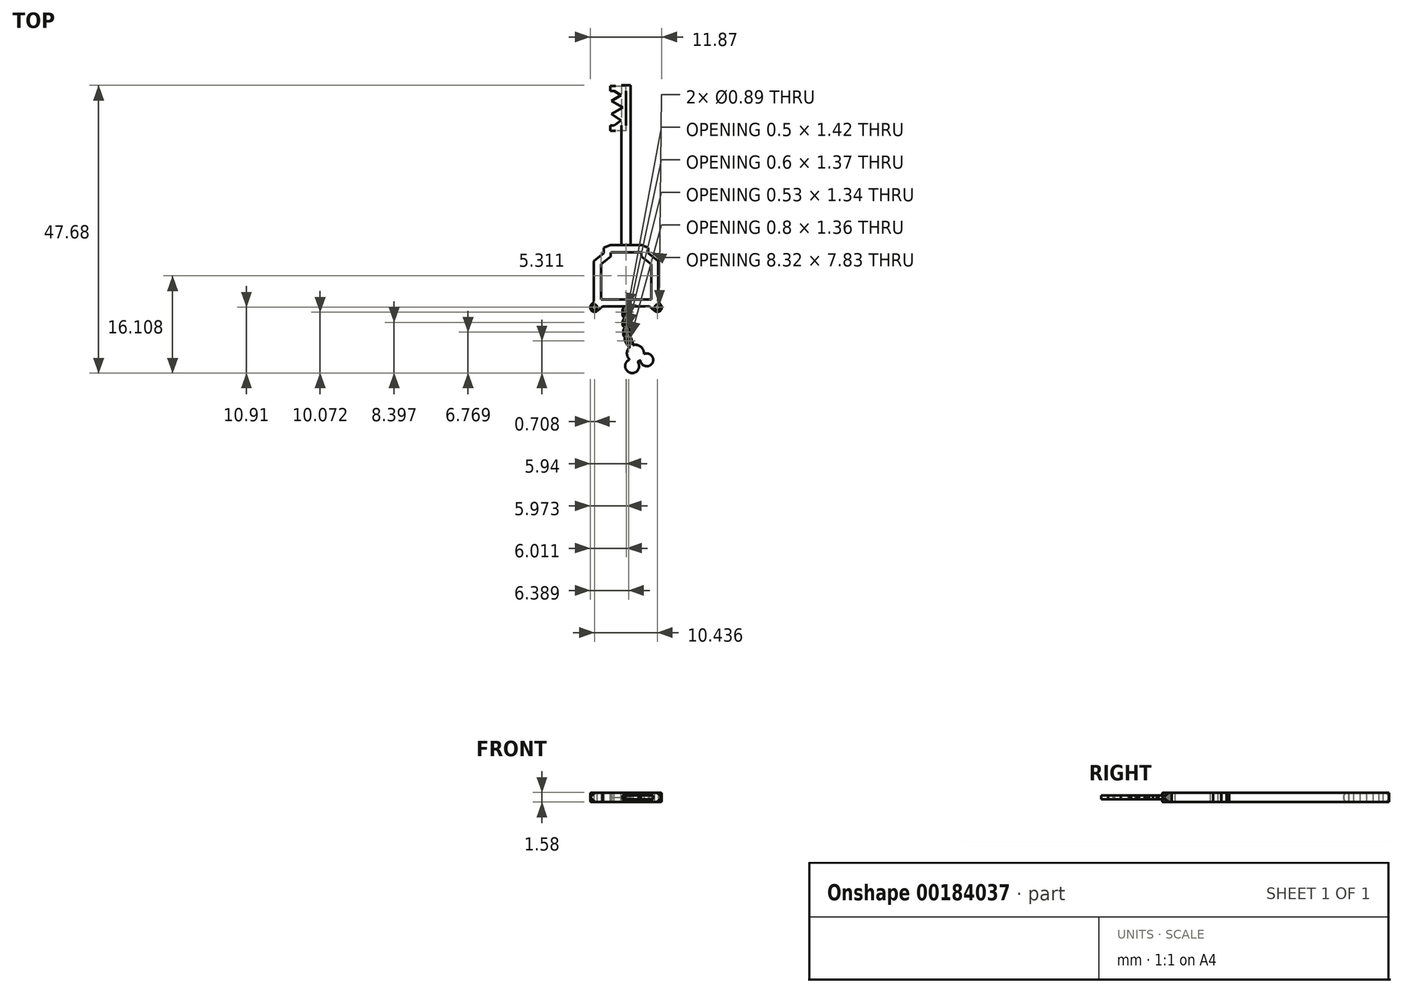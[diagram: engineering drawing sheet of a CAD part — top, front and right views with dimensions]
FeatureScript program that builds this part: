
annotation { "Feature Type Name" : "Feature", "Feature Type Description" : "" }
export const myFeature = defineFeature(function(context is Context, id is Id, definition is map)
    precondition{}
    {
        {
            var Q0;
            Q0=qCreatedBy(makeId("Top.planeOp"),FACE);
            var sketch = newSketch(context, id + "F0", { "sketchPlane" : qUnion([Q0])});
            skLineSegment(sketch, "E0.bottom", {"start": v(0, 26.39) * mm, "end": v(-3.39, 26.39) * mm});
            skLineSegment(sketch, "E0.top", {"start": v(0, 18.97) * mm, "end": v(-3.39, 18.97) * mm});
            skLineSegment(sketch, "E0.left", {"start": v(0, 26.39) * mm, "end": v(0, 18.97) * mm});
            skLineSegment(sketch, "E0.right", {"start": v(-3.39, 26.39) * mm, "end": v(-3.39, 18.97) * mm});
            skSolve(sketch);
        }
        {
            var Q0;
            Q0=makeQuery(id+"F0.imprint","IMPRINT",FACE,{"disambiguationData":[TD([[makeQuery(id+"F0.imprint","IMPRINT",EDGE,{"derivedFrom":sQuery(id+"F0.wireOp",EDGE,"E0.bottom")}),1.0]])]});
            extrude(context, id + "F1", {"entities" : qUnion([Q0]), "endBound" : BoundingType.SYMMETRIC, "depth" : 1.57 * mm});
        }
        {
            var Q0;
            Q0=makeQuery(id+"F1.opExtrude","CAP_EDGE",EDGE,{"disambiguationData":[OSD([sQuery(id+"F0.wireOp",EDGE,"E0.top")])],"isStart":false});
            var Q1;
            Q1=makeQuery(id+"F1.opExtrude","CAP_EDGE",EDGE,{"disambiguationData":[OSD([sQuery(id+"F0.wireOp",EDGE,"E0.top")])],"isStart":true});
            var Q2;
            Q2=makeQuery(id+"F1.opExtrude","CAP_EDGE",EDGE,{"disambiguationData":[OSD([sQuery(id+"F0.wireOp",EDGE,"E0.bottom")])],"isStart":false});
            var Q3;
            Q3=makeQuery(id+"F1.opExtrude","CAP_EDGE",EDGE,{"disambiguationData":[OSD([sQuery(id+"F0.wireOp",EDGE,"E0.bottom")])],"isStart":true});
            fillet(context, id + "F2", {"entities" : qUnion([Q0, Q1, Q2, Q3]), "radius" : 0.86 * mm, "tangentPropagation" : true, "rho" : 0.5, "crossSection" : FilletCrossSection.CONIC, "allowEdgeOverflow" : false});
        }
        {
            var Q0;
            Q0=makeQuery(id+"F1.opExtrude","CAP_FACE",FACE,{"disambiguationData":[OSD([sQuery(id+"F0.wireOp",EDGE,"E0.bottom"),sQuery(id+"F0.wireOp",EDGE,"E0.top"),sQuery(id+"F0.wireOp",EDGE,"E0.left"),sQuery(id+"F0.wireOp",EDGE,"E0.right")])],"isStart":false});
            var sketch = newSketch(context, id + "F3", { "sketchPlane" : qUnion([Q0])});
            skLineSegment(sketch, "E1", {"start": v(-3.39, 25.53) * mm, "end": v(-1.97, 25.53) * mm});
            skLineSegment(sketch, "E2", {"start": v(-1.97, 25.53) * mm, "end": v(-0.83, 24.86) * mm});
            skLineSegment(sketch, "E3", {"start": v(-0.83, 24.86) * mm, "end": v(-2.39, 23.92) * mm});
            skLineSegment(sketch, "E4", {"start": v(-2.39, 23.92) * mm, "end": v(-0.52, 22.82) * mm});
            skLineSegment(sketch, "E5", {"start": v(-0.52, 22.82) * mm, "end": v(-2.39, 21.74) * mm});
            skLineSegment(sketch, "E6", {"start": v(-2.39, 21.74) * mm, "end": v(-0.83, 20.67) * mm});
            skLineSegment(sketch, "E7", {"start": v(-0.83, 20.67) * mm, "end": v(-2, 19.83) * mm});
            skLineSegment(sketch, "E8", {"start": v(-2, 19.83) * mm, "end": v(-3.39, 19.83) * mm});
            skLineSegment(sketch, "E9", {"start": v(-3.39, 19.83) * mm, "end": v(-3.39, 25.53) * mm});
            skSolve(sketch);
        }
        {
            var Q0;
            Q0=makeQuery(id+"F3.imprint","IMPRINT",FACE,{"disambiguationData":[TD([[makeQuery(id+"F3.imprint","IMPRINT",EDGE,{"derivedFrom":sQuery(id+"F3.wireOp",EDGE,"E1")}),1.0]])]});
            extrude(context, id + "F4", {"entities" : qUnion([Q0]), "operationType" : NewBodyOperationType.REMOVE, "oppositeDirection" : true, "depth" : 2.54 * mm});
        }
        {
            var Q0;
            Q0=qCreatedBy(makeId("Top.planeOp"),FACE);
            var sketch = newSketch(context, id + "F5", { "sketchPlane" : qUnion([Q0])});
            skLineSegment(sketch, "E10", {"start": v(0, 0) * mm, "end": v(-2.6, 0) * mm});
            skLineSegment(sketch, "E11", {"start": v(-2.6, 0) * mm, "end": v(-3.7, -0.44) * mm});
            skLineSegment(sketch, "E12", {"start": v(-3.7, -0.44) * mm, "end": v(-3.7, -1.33) * mm});
            skLineSegment(sketch, "E13", {"start": v(-3.7, -1.33) * mm, "end": v(-5.33, -2.62) * mm});
            skLineSegment(sketch, "E14", {"start": v(-5.33, -2.62) * mm, "end": v(-5.33, -9.54) * mm});
            skLineSegment(sketch, "E15", {"start": v(-5.33, -9.54) * mm, "end": v(-6.2, -10.17) * mm});
            skLineSegment(sketch, "E16", {"start": v(-6.2, -10.17) * mm, "end": v(-5.33, -11.38) * mm});
            skLineSegment(sketch, "E17", {"start": v(-5.33, -11.38) * mm, "end": v(-3.9, -10.17) * mm});
            skLineSegment(sketch, "E18", {"start": v(-3.9, -10.17) * mm, "end": v(0, -10.17) * mm});
            skLineSegment(sketch, "E19.MirrorCS", {"start": v(2.6, 0) * mm, "end": v(3.7, -0.44) * mm});
            skLineSegment(sketch, "E20.MirrorCS", {"start": v(3.7, -0.44) * mm, "end": v(3.7, -1.33) * mm});
            skLineSegment(sketch, "E21.MirrorCS", {"start": v(3.7, -1.33) * mm, "end": v(5.33, -2.62) * mm});
            skLineSegment(sketch, "E22.MirrorCS", {"start": v(5.33, -2.62) * mm, "end": v(5.33, -9.54) * mm});
            skLineSegment(sketch, "E23.MirrorCS", {"start": v(5.33, -9.54) * mm, "end": v(6.2, -10.17) * mm});
            skLineSegment(sketch, "E24.MirrorCS", {"start": v(6.2, -10.17) * mm, "end": v(5.33, -11.38) * mm});
            skLineSegment(sketch, "E25.MirrorCS", {"start": v(5.33, -11.38) * mm, "end": v(3.9, -10.17) * mm});
            skLineSegment(sketch, "E26.MirrorCS", {"start": v(3.9, -10.17) * mm, "end": v(0, -10.17) * mm});
            skLineSegment(sketch, "E27.MirrorCS", {"start": v(0, 0) * mm, "end": v(2.6, 0) * mm});
            skLineSegment(sketch, "E28.0", {"start": v(2.52, -1.17) * mm, "end": v(2.52, -1.9) * mm});
            skLineSegment(sketch, "E28.1", {"start": v(-2.52, -1.23) * mm, "end": v(-2.52, -1.9) * mm});
            skLineSegment(sketch, "E28.2", {"start": v(-2.37, -1.17) * mm, "end": v(-2.52, -1.23) * mm});
            skLineSegment(sketch, "E28.3", {"start": v(0, -1.17) * mm, "end": v(-2.37, -1.17) * mm});
            skLineSegment(sketch, "E28.4", {"start": v(0, -1.17) * mm, "end": v(2.52, -1.17) * mm});
            skLineSegment(sketch, "E28.5", {"start": v(-2.52, -1.9) * mm, "end": v(-4.16, -3.19) * mm});
            skLineSegment(sketch, "E28.6", {"start": v(-4.16, -3.19) * mm, "end": v(-4.16, -9) * mm});
            skLineSegment(sketch, "E28.7", {"start": v(-4.16, -9) * mm, "end": v(0, -9) * mm});
            skLineSegment(sketch, "E28.8", {"start": v(4.16, -9) * mm, "end": v(0, -9) * mm});
            skLineSegment(sketch, "E28.9", {"start": v(4.16, -3.19) * mm, "end": v(4.16, -9) * mm});
            skLineSegment(sketch, "E28.10", {"start": v(2.52, -1.9) * mm, "end": v(4.16, -3.19) * mm});
            skSolve(sketch);
        }
        {
            var Q0;
            Q0=makeQuery(id+"F5.imprint","IMPRINT",FACE,{"disambiguationData":[TD([[makeQuery(id+"F5.imprint","IMPRINT",EDGE,{"derivedFrom":sQuery(id+"F5.wireOp",EDGE,"E10")}),1.0]])]});
            extrude(context, id + "F6", {"entities" : qUnion([Q0]), "endBound" : BoundingType.SYMMETRIC, "depth" : 1.57 * mm});
        }
        {
            var Q0;
            Q0=qCreatedBy(makeId("Top.planeOp"),FACE);
            var sketch = newSketch(context, id + "F7", { "sketchPlane" : qUnion([Q0])});
            skLineSegment(sketch, "E29", {"start": v(0.52, -8.98) * mm, "end": v(0.52, -1.2) * mm});
            skSolve(sketch);
        }
        {
            var Q0;
            Q0=qCreatedBy(makeId("Top.planeOp"),FACE);
            var sketch = newSketch(context, id + "F8", { "sketchPlane" : qUnion([Q0])});
            skLineSegment(sketch, "E30", {"start": v(0, -1.2) * mm, "end": v(0, -8.98) * mm});
            skSolve(sketch);
        }
        {
            var Q0;
            Q0=sQuery(id+"F7.wireOp",EDGE,"E29");
            var Q1;
            Q1=sQuery(id+"F8.wireOp",EDGE,"E30");
            revolve(context, id + "F9", {"bodyType" : ToolBodyType.SURFACE, "surfaceEntities" : qUnion([Q0]), "axis" : qUnion([Q1]), "revolveType" : RevolveType.FULL});
        }
        {
            var Q0;
            Q0=qCreatedBy(makeId("Top.planeOp"),FACE);
            var sketch = newSketch(context, id + "F10", { "sketchPlane" : qUnion([Q0])});
            skLineSegment(sketch, "E31", {"start": v(0, -10.03) * mm, "end": v(-0.55, -10.56) * mm});
            skLineSegment(sketch, "E32", {"start": v(-0.55, -10.56) * mm, "end": v(-0.55, -11.72) * mm});
            skLineSegment(sketch, "E33", {"start": v(-0.55, -11.72) * mm, "end": v(0, -12.3) * mm});
            skLineSegment(sketch, "E34", {"start": v(0, -12.3) * mm, "end": v(0.61, -11.72) * mm});
            skLineSegment(sketch, "E35", {"start": v(0.61, -11.72) * mm, "end": v(0.61, -10.24) * mm});
            skLineSegment(sketch, "E36", {"start": v(0.61, -10.24) * mm, "end": v(0, -10.03) * mm});
            skLineSegment(sketch, "E37", {"start": v(-0.27, -12) * mm, "end": v(-0.55, -12.63) * mm});
            skLineSegment(sketch, "E38", {"start": v(-0.55, -12.63) * mm, "end": v(-0.55, -13.3) * mm});
            skLineSegment(sketch, "E39", {"start": v(-0.55, -13.3) * mm, "end": v(0, -13.87) * mm});
            skLineSegment(sketch, "E40", {"start": v(0, -13.87) * mm, "end": v(0.61, -13.3) * mm});
            skLineSegment(sketch, "E41", {"start": v(0.61, -13.3) * mm, "end": v(0.61, -12.63) * mm});
            skLineSegment(sketch, "E42", {"start": v(0.61, -12.63) * mm, "end": v(0.3, -11.72) * mm});
            skPoint(sketch, "E42.endSnap0", {"position": v(0.3, -12) * mm});
            skLineSegment(sketch, "E43", {"start": v(0.3, -11.72) * mm, "end": v(-0.27, -12) * mm});
            skLineSegment(sketch, "E44", {"start": v(0, -13.3) * mm, "end": v(0.61, -13.94) * mm});
            skLineSegment(sketch, "E45", {"start": v(0.61, -13.94) * mm, "end": v(0.61, -14.95) * mm});
            skLineSegment(sketch, "E46", {"start": v(0.61, -14.95) * mm, "end": v(0, -15.49) * mm});
            skLineSegment(sketch, "E47", {"start": v(0, -15.49) * mm, "end": v(-0.47, -14.95) * mm});
            skLineSegment(sketch, "E48", {"start": v(-0.47, -14.95) * mm, "end": v(-0.47, -14.08) * mm});
            skLineSegment(sketch, "E49", {"start": v(-0.47, -14.08) * mm, "end": v(0, -13.3) * mm});
            skLineSegment(sketch, "E50", {"start": v(0.27, -14.72) * mm, "end": v(0.81, -15.35) * mm});
            skLineSegment(sketch, "E51", {"start": v(0.81, -15.35) * mm, "end": v(1.13, -16.25) * mm});
            skLineSegment(sketch, "E52", {"start": v(1.13, -16.25) * mm, "end": v(1.13, -16.97) * mm});
            skLineSegment(sketch, "E53", {"start": v(1.13, -16.97) * mm, "end": v(0.25, -16.63) * mm});
            skLineSegment(sketch, "E54", {"start": v(0.25, -16.63) * mm, "end": v(-0.27, -15.66) * mm});
            skLineSegment(sketch, "E55", {"start": v(-0.27, -15.66) * mm, "end": v(0.27, -14.72) * mm});
            skCircle(sketch, "E56", {"center": v(1.56, -17.92) * mm, "radius": 1.41 * mm});
            skCircle(sketch, "E57", {"center": v(3.44, -19) * mm, "radius": 1.07 * mm});
            skCircle(sketch, "E58", {"center": v(1.01, -20.03) * mm, "radius": 1.16 * mm});
            skLineSegment(sketch, "E59.0", {"start": v(0.09, -10.4) * mm, "end": v(-0.22, -10.7) * mm});
            skLineSegment(sketch, "E59.1", {"start": v(-0.22, -11.59) * mm, "end": v(0.01, -11.83) * mm});
            skLineSegment(sketch, "E59.2", {"start": v(0.01, -11.83) * mm, "end": v(0.28, -11.58) * mm});
            skLineSegment(sketch, "E59.3", {"start": v(-0.22, -10.7) * mm, "end": v(-0.22, -11.59) * mm});
            skLineSegment(sketch, "E59.4", {"start": v(0.28, -11.58) * mm, "end": v(0.28, -10.47) * mm});
            skLineSegment(sketch, "E59.5", {"start": v(0.28, -10.47) * mm, "end": v(0.09, -10.4) * mm});
            skLineSegment(sketch, "E60.0", {"start": v(-0.27, -12.69) * mm, "end": v(-0.27, -13.18) * mm});
            skLineSegment(sketch, "E60.1", {"start": v(-0.06, -12.21) * mm, "end": v(-0.27, -12.69) * mm});
            skLineSegment(sketch, "E60.2", {"start": v(0.01, -13.48) * mm, "end": v(0.33, -13.17) * mm});
            skLineSegment(sketch, "E60.3", {"start": v(0.33, -13.17) * mm, "end": v(0.33, -12.67) * mm});
            skLineSegment(sketch, "E60.4", {"start": v(0.33, -12.67) * mm, "end": v(0.14, -12.11) * mm});
            skLineSegment(sketch, "E60.5", {"start": v(-0.27, -13.18) * mm, "end": v(0.01, -13.48) * mm});
            skLineSegment(sketch, "E60.6", {"start": v(0.14, -12.11) * mm, "end": v(-0.06, -12.21) * mm});
            skLineSegment(sketch, "E61.0", {"start": v(0.03, -15.1) * mm, "end": v(-0.2, -14.84) * mm});
            skLineSegment(sketch, "E61.1", {"start": v(-0.2, -14.16) * mm, "end": v(0.05, -13.75) * mm});
            skLineSegment(sketch, "E61.2", {"start": v(0.05, -13.75) * mm, "end": v(0.33, -14.05) * mm});
            skLineSegment(sketch, "E61.3", {"start": v(-0.2, -14.84) * mm, "end": v(-0.2, -14.16) * mm});
            skLineSegment(sketch, "E61.4", {"start": v(0.33, -14.05) * mm, "end": v(0.33, -14.82) * mm});
            skLineSegment(sketch, "E61.5", {"start": v(0.33, -14.82) * mm, "end": v(0.03, -15.1) * mm});
            skLineSegment(sketch, "E62.0", {"start": v(0.85, -16.56) * mm, "end": v(0.45, -16.4) * mm});
            skLineSegment(sketch, "E62.1", {"start": v(0.05, -15.66) * mm, "end": v(0.31, -15.2) * mm});
            skLineSegment(sketch, "E62.2", {"start": v(0.31, -15.2) * mm, "end": v(0.57, -15.5) * mm});
            skLineSegment(sketch, "E62.3", {"start": v(0.45, -16.4) * mm, "end": v(0.05, -15.66) * mm});
            skLineSegment(sketch, "E62.4", {"start": v(0.57, -15.5) * mm, "end": v(0.85, -16.3) * mm});
            skLineSegment(sketch, "E62.5", {"start": v(0.85, -16.3) * mm, "end": v(0.85, -16.56) * mm});
            skSolve(sketch);
        }
        {
            var Q0;
            Q0 = qSketchRegion(id + "F10", true);
            extrude(context, id + "F11", {"entities" : qUnion([Q0]), "endBound" : BoundingType.SYMMETRIC, "depth" : 0.64 * mm});
        }
        {
            var Q0;
            Q0=makeQuery(id+"F6.opExtrude","CAP_FACE",FACE,{"disambiguationData":[OSD([sQuery(id+"F5.wireOp",EDGE,"E10"),sQuery(id+"F5.wireOp",EDGE,"E11"),sQuery(id+"F5.wireOp",EDGE,"E12"),sQuery(id+"F5.wireOp",EDGE,"E13"),sQuery(id+"F5.wireOp",EDGE,"E14"),sQuery(id+"F5.wireOp",EDGE,"E15"),sQuery(id+"F5.wireOp",EDGE,"E16"),sQuery(id+"F5.wireOp",EDGE,"E17"),sQuery(id+"F5.wireOp",EDGE,"E18"),sQuery(id+"F5.wireOp",EDGE,"E20.MirrorCS"),sQuery(id+"F5.wireOp",EDGE,"E21.MirrorCS"),sQuery(id+"F5.wireOp",EDGE,"E22.MirrorCS"),sQuery(id+"F5.wireOp",EDGE,"E23.MirrorCS"),sQuery(id+"F5.wireOp",EDGE,"E24.MirrorCS"),sQuery(id+"F5.wireOp",EDGE,"E25.MirrorCS"),sQuery(id+"F5.wireOp",EDGE,"E26.MirrorCS"),sQuery(id+"F5.wireOp",EDGE,"E19.MirrorCS"),sQuery(id+"F5.wireOp",EDGE,"E27.MirrorCS"),sQuery(id+"F5.wireOp",EDGE,"E28.0"),sQuery(id+"F5.wireOp",EDGE,"E28.1"),sQuery(id+"F5.wireOp",EDGE,"E28.2"),sQuery(id+"F5.wireOp",EDGE,"E28.3"),sQuery(id+"F5.wireOp",EDGE,"E28.4"),sQuery(id+"F5.wireOp",EDGE,"E28.5"),sQuery(id+"F5.wireOp",EDGE,"E28.6"),sQuery(id+"F5.wireOp",EDGE,"E28.7"),sQuery(id+"F5.wireOp",EDGE,"E28.8"),sQuery(id+"F5.wireOp",EDGE,"E28.9"),sQuery(id+"F5.wireOp",EDGE,"E28.10")])],"isStart":false});
            var sketch = newSketch(context, id + "F12", { "sketchPlane" : qUnion([Q0])});
            skPoint(sketch, "E63", {"position": v(-5.23, -10.28) * mm});
            skPoint(sketch, "E64", {"position": v(5.2, -10.28) * mm});
            skSolve(sketch);
        }
        {
            var Q0;
            Q0=sQuery(id+"F12.wireOp",VERTEX,"E63");
            var Q1;
            Q1=sQuery(id+"F12.wireOp",VERTEX,"E64");
            var Q2;
            Q2=makeQuery(id+"F6.opExtrude","SWEPT_BODY",BODY,{"disambiguationData":[OSD([sQuery(id+"F5.wireOp",EDGE,"E10"),sQuery(id+"F5.wireOp",EDGE,"E11"),sQuery(id+"F5.wireOp",EDGE,"E12"),sQuery(id+"F5.wireOp",EDGE,"E13"),sQuery(id+"F5.wireOp",EDGE,"E14"),sQuery(id+"F5.wireOp",EDGE,"E15"),sQuery(id+"F5.wireOp",EDGE,"E16"),sQuery(id+"F5.wireOp",EDGE,"E17"),sQuery(id+"F5.wireOp",EDGE,"E18"),sQuery(id+"F5.wireOp",EDGE,"E20.MirrorCS"),sQuery(id+"F5.wireOp",EDGE,"E21.MirrorCS"),sQuery(id+"F5.wireOp",EDGE,"E22.MirrorCS"),sQuery(id+"F5.wireOp",EDGE,"E23.MirrorCS"),sQuery(id+"F5.wireOp",EDGE,"E24.MirrorCS"),sQuery(id+"F5.wireOp",EDGE,"E25.MirrorCS"),sQuery(id+"F5.wireOp",EDGE,"E26.MirrorCS"),sQuery(id+"F5.wireOp",EDGE,"E19.MirrorCS"),sQuery(id+"F5.wireOp",EDGE,"E27.MirrorCS"),sQuery(id+"F5.wireOp",EDGE,"E28.0"),sQuery(id+"F5.wireOp",EDGE,"E28.1"),sQuery(id+"F5.wireOp",EDGE,"E28.2"),sQuery(id+"F5.wireOp",EDGE,"E28.3"),sQuery(id+"F5.wireOp",EDGE,"E28.4"),sQuery(id+"F5.wireOp",EDGE,"E28.5"),sQuery(id+"F5.wireOp",EDGE,"E28.6"),sQuery(id+"F5.wireOp",EDGE,"E28.7"),sQuery(id+"F5.wireOp",EDGE,"E28.8"),sQuery(id+"F5.wireOp",EDGE,"E28.9"),sQuery(id+"F5.wireOp",EDGE,"E28.10")])]});
            hole(context, id + "F13", {"style" : HoleStyle.SIMPLE, "endStyle" : HoleEndStyle.THROUGH, "holeDiameter" : 0.89 * mm, "locations" : qUnion([Q0, Q1]), "scope" : qUnion([Q2]), "isTappedThrough" : true});
        }
        {
            var Q0;
            Q0=makeQuery(id+"F4.boolean.opBoolean","SPLIT",FACE,{"disambiguationData":[TD([makeQuery(id+"F4.opExtrude","SWEPT_FACE",FACE,{"disambiguationData":[OSD([sQuery(id+"F3.wireOp",EDGE,"E8")])]})])],"derivedFrom":makeQuery(id+"F1.opExtrude","SWEPT_FACE",FACE,{"disambiguationData":[OSD([sQuery(id+"F0.wireOp",EDGE,"E0.right")])]})});
            extrude(context, id + "F14", {"entities" : qUnion([Q0]), "operationType" : NewBodyOperationType.REMOVE, "oppositeDirection" : true, "depth" : 0.76 * mm});
        }
        {
            var Q0;
            Q0=makeQuery(id+"F4.boolean.opBoolean","SPLIT",FACE,{"disambiguationData":[TD([makeQuery(id+"F4.opExtrude","SWEPT_FACE",FACE,{"disambiguationData":[OSD([sQuery(id+"F3.wireOp",EDGE,"E1")])]})])],"derivedFrom":makeQuery(id+"F1.opExtrude","SWEPT_FACE",FACE,{"disambiguationData":[OSD([sQuery(id+"F0.wireOp",EDGE,"E0.right")])]})});
            var Q1;
            Q1 = qSketchRegion(id + "F12", true);
            extrude(context, id + "F15", {"entities" : qUnion([Q0, Q1]), "operationType" : NewBodyOperationType.REMOVE, "oppositeDirection" : true, "depth" : 0.76 * mm});
        }
        {
            var Q0;
            Q0=makeQuery(id+"F6.opExtrude","SWEPT_FACE",FACE,{"disambiguationData":[OSD([sQuery(id+"F5.wireOp",EDGE,"E10"),sQuery(id+"F5.wireOp",EDGE,"E27.MirrorCS")])]});
            var sketch = newSketch(context, id + "F16", { "sketchPlane" : qUnion([Q0])});
            skCircle(sketch, "E65", {"center": v(0, 0) * mm, "radius": 0.77 * mm});
            skSolve(sketch);
        }
        {
            var Q0;
            Q0 = qSketchRegion(id + "F16", true);
            extrude(context, id + "F17", {"entities" : qUnion([Q0]), "depth" : 26.5 * mm});
        }
        {
            var Q0;
            Q0=makeQuery(id+"F6.opExtrude","SWEPT_FACE",FACE,{"disambiguationData":[OSD([sQuery(id+"F5.wireOp",EDGE,"E16")])]});
            fillet(context, id + "F18", {"entities" : qUnion([Q0]), "radius" : 0.67 * mm, "tangentPropagation" : true, "allowEdgeOverflow" : false});
        }
        {
            var Q0;
            Q0=makeQuery(id+"F6.opExtrude","SWEPT_FACE",FACE,{"disambiguationData":[OSD([sQuery(id+"F5.wireOp",EDGE,"E24.MirrorCS")])]});
            fillet(context, id + "F19", {"entities" : qUnion([Q0]), "radius" : 0.7 * mm, "tangentPropagation" : true, "allowEdgeOverflow" : false});
        }
    });
